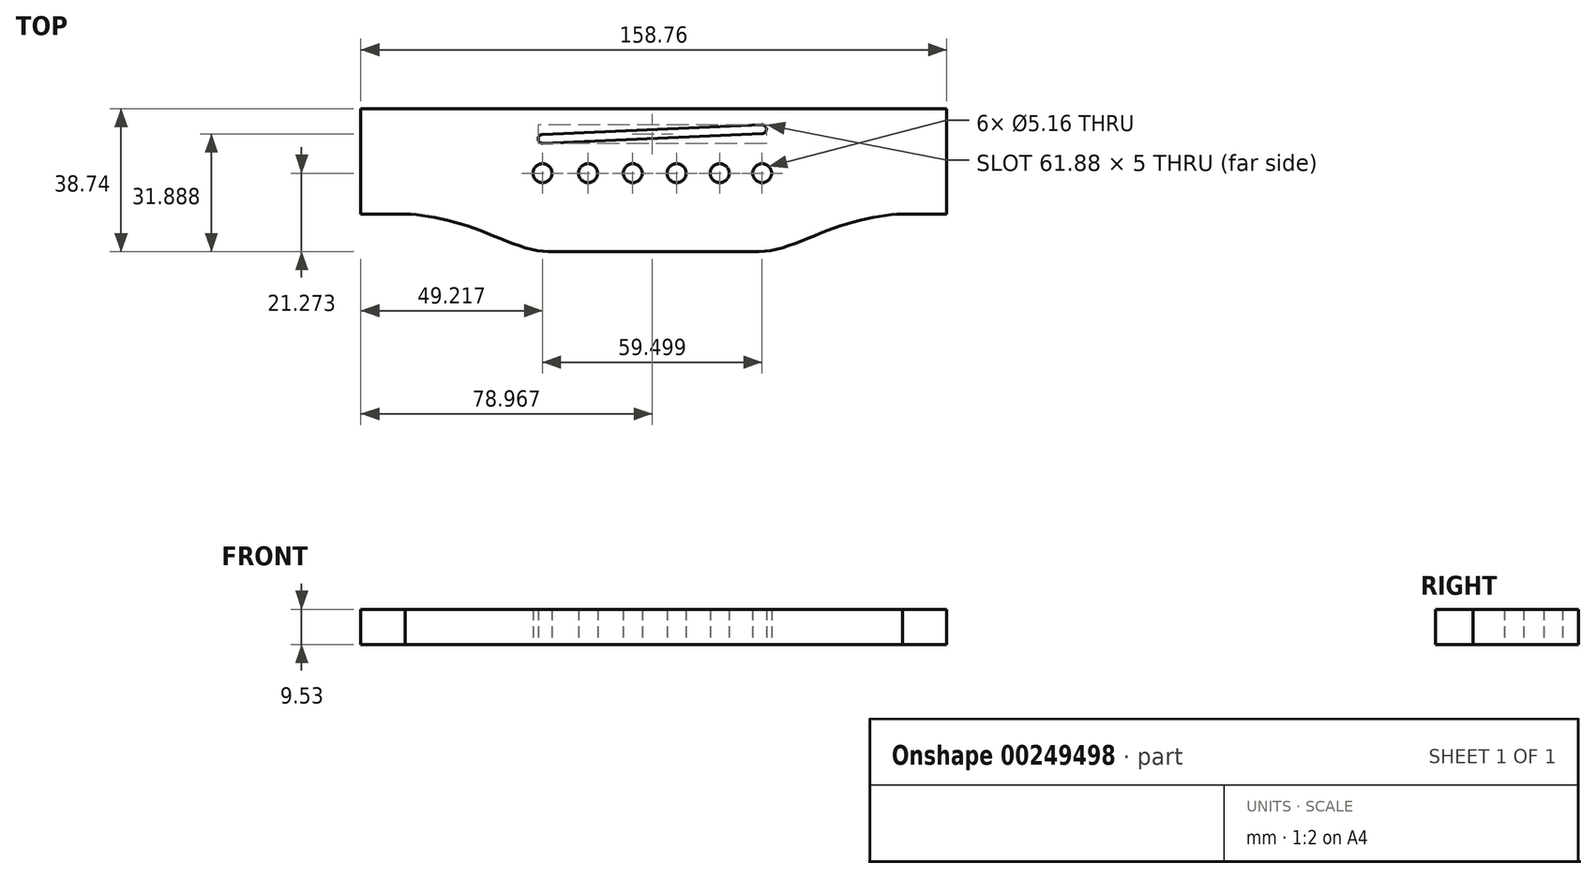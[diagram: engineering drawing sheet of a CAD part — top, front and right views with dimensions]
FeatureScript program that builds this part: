
annotation { "Feature Type Name" : "Feature", "Feature Type Description" : "" }
export const myFeature = defineFeature(function(context is Context, id is Id, definition is map)
    precondition{}
    {
        {
            var Q0;
            Q0=qCreatedBy(makeId("Top.planeOp"),FACE);
            var sketch = newSketch(context, id + "F0", { "sketchPlane" : qUnion([Q0])});
            skLineSegment(sketch, "E0", {"start": v(0, 41.58) * mm, "end": v(0, -43.57) * mm, "construction": true});
            skLineSegment(sketch, "E1", {"start": v(0, 38.73) * mm, "end": v(-79.38, 38.73) * mm});
            skLineSegment(sketch, "E2", {"start": v(-79.38, 38.73) * mm, "end": v(-79.38, 10.16) * mm});
            skLineSegment(sketch, "E3", {"start": v(0, 0) * mm, "end": v(-28.58, 0) * mm});
            skCircle(sketch, "E4", {"center": v(-30.16, 21.27) * mm, "radius": 2.58 * mm});
            skCircle(sketch, "E5.MirrorC", {"center": v(29.34, 21.27) * mm, "radius": 2.58 * mm});
            skLineSegment(sketch, "E6.MirrorCS", {"start": v(0, 38.73) * mm, "end": v(79.38, 38.73) * mm});
            skLineSegment(sketch, "E7.MirrorCS", {"start": v(79.38, 38.73) * mm, "end": v(79.38, 7.14) * mm});
            skLineSegment(sketch, "E8.MirrorCS", {"start": v(0, 0) * mm, "end": v(28.58, 0) * mm});
            skCircle(sketch, "E9", {"center": v(-17.8, 21.27) * mm, "radius": 2.58 * mm});
            skCircle(sketch, "E10", {"center": v(6.16, 21.27) * mm, "radius": 2.58 * mm});
            skCircle(sketch, "E11", {"center": v(17.83, 21.27) * mm, "radius": 2.58 * mm});
            skLineSegment(sketch, "E12", {"start": v(-66.56, 21.27) * mm, "end": v(70.4, 21.27) * mm, "construction": true});
            skCircle(sketch, "E13", {"center": v(-5.7, 21.27) * mm, "radius": 2.58 * mm});
            skCircle(sketch, "E14", {"center": v(-30.16, 21.27) * mm, "radius": 0.67 * mm});
            skCircle(sketch, "E15", {"center": v(-17.8, 21.27) * mm, "radius": 0.53 * mm});
            skCircle(sketch, "E16", {"center": v(-5.7, 21.27) * mm, "radius": 0.4 * mm});
            skCircle(sketch, "E17", {"center": v(6.16, 21.27) * mm, "radius": 0.3 * mm});
            skCircle(sketch, "E18", {"center": v(17.83, 21.27) * mm, "radius": 0.2 * mm});
            skCircle(sketch, "E19", {"center": v(29.34, 21.27) * mm, "radius": 0.15 * mm});
            skLineSegment(sketch, "E20", {"start": v(-79.38, 10.16) * mm, "end": v(-79.38, 7.14) * mm});
            skLineSegment(sketch, "E21", {"start": v(-79.38, 10.16) * mm, "end": v(-67.32, 10.16) * mm});
            skFitSpline(sketch, "E22", {"points": [v(-67.32, 10.16) * mm, v(-47.85, 6.02) * mm, v(-28.58, 0) * mm], "startDerivative": vector(32.7, -0.39) * mm, "endDerivative": vector(34, 0) * mm});
            skFitSpline(sketch, "E23.MirrorCS", {"points": [v(67.32, 10.16) * mm, v(47.85, 6.02) * mm, v(28.58, 0) * mm], "startDerivative": vector(-32.7, -0.39) * mm, "endDerivative": vector(-34, 0) * mm});
            skLineSegment(sketch, "E24.MirrorCS", {"start": v(79.38, 10.16) * mm, "end": v(67.32, 10.16) * mm});
            skLineSegment(sketch, "E25", {"start": v(-30.16, 21.27) * mm, "end": v(-30.16, 38.73) * mm, "construction": true});
            skLineSegment(sketch, "E26", {"start": v(-17.8, 21.27) * mm, "end": v(-17.8, 38.73) * mm, "construction": true});
            skLineSegment(sketch, "E27", {"start": v(-5.7, 21.27) * mm, "end": v(-5.7, 38.73) * mm, "construction": true});
            skLineSegment(sketch, "E28", {"start": v(6.16, 21.27) * mm, "end": v(6.16, 38.73) * mm, "construction": true});
            skLineSegment(sketch, "E29", {"start": v(17.83, 21.27) * mm, "end": v(17.83, 38.73) * mm, "construction": true});
            skLineSegment(sketch, "E30", {"start": v(29.34, 21.27) * mm, "end": v(29.34, 38.73) * mm, "construction": true});
            skPoint(sketch, "E31", {"position": v(-30.16, 29.39) * mm});
            skPoint(sketch, "E32", {"position": v(-17.8, 32.44) * mm});
            skPoint(sketch, "E33", {"position": v(-5.7, 33.15) * mm});
            skPoint(sketch, "E34", {"position": v(6.16, 33.12) * mm});
            skPoint(sketch, "E35", {"position": v(17.83, 30.86) * mm});
            skPoint(sketch, "E36", {"position": v(29.34, 33.2) * mm});
            skArc(sketch, "E37", {"start": v(-30.16, 31.77) * mm, "mid": v(-31.35, 30.55) * mm, "end": v(-30.11, 29.39) * mm});
            skArc(sketch, "E38", {"start": v(29.34, 32) * mm, "mid": v(30.53, 33.22) * mm, "end": v(29.28, 34.39) * mm});
            skLineSegment(sketch, "E39", {"start": v(-30.21, 31.77) * mm, "end": v(29.28, 34.39) * mm});
            skLineSegment(sketch, "E40", {"start": v(-30.11, 29.39) * mm, "end": v(29.39, 32) * mm});
            skSolve(sketch);
        }
        {
            var Q0;
            Q0=makeQuery(id+"F0.imprint","IMPRINT",FACE,{"disambiguationData":[TD([[makeQuery(id+"F0.imprint","IMPRINT",EDGE,{"derivedFrom":sQuery(id+"F0.wireOp",EDGE,"E1")}),1.0]])]});
            extrude(context, id + "F1", {"entities" : qUnion([Q0]), "depth" : 9.52 * mm});
        }
    });
